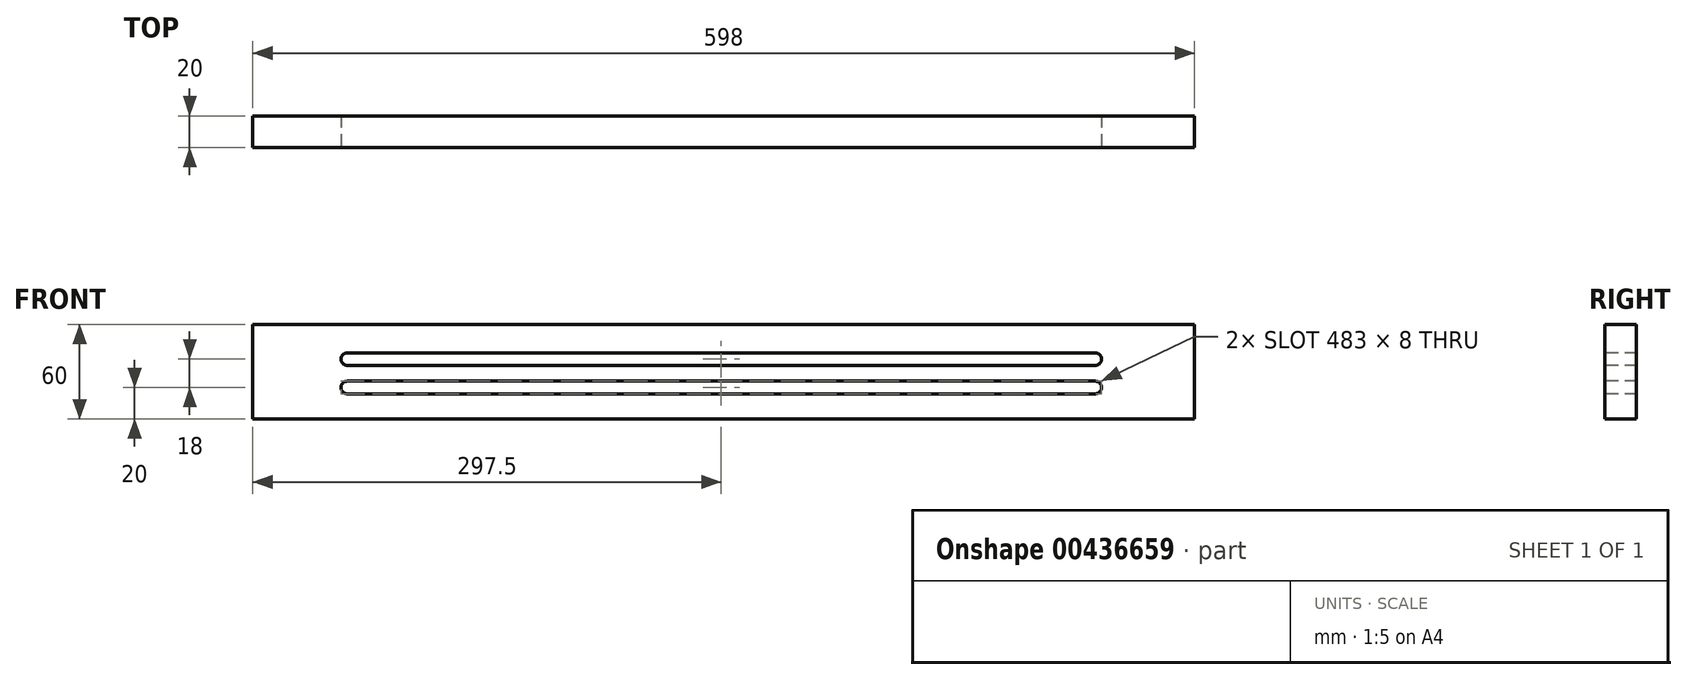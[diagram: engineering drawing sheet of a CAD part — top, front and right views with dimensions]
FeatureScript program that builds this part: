
annotation { "Feature Type Name" : "Feature", "Feature Type Description" : "" }
export const myFeature = defineFeature(function(context is Context, id is Id, definition is map)
    precondition{}
    {
        {
            var Q0;
            Q0=qCreatedBy(makeId("Right.planeOp"),FACE);
            var sketch = newSketch(context, id + "F0", { "sketchPlane" : qUnion([Q0])});
            skLineSegment(sketch, "E0.bottom", {"start": v(10, -30) * mm, "end": v(-10, -30) * mm});
            skLineSegment(sketch, "E0.top", {"start": v(10, 30) * mm, "end": v(-10, 30) * mm});
            skLineSegment(sketch, "E0.left", {"start": v(10, -30) * mm, "end": v(10, 30) * mm});
            skLineSegment(sketch, "E0.right", {"start": v(-10, -30) * mm, "end": v(-10, 30) * mm});
            skPoint(sketch, "E0.middle", {"position": v(0, 0) * mm});
            skSolve(sketch);
        }
        {
            var Q0;
            Q0=qSketchRegion(id+"F0",true);
            extrude(context, id + "F1", {"entities" : qUnion([Q0]), "depth" : 598 * mm});
        }
        {
            var Q0;
            Q0=makeQuery(id+"F1.opExtrude","SWEPT_FACE",FACE,{"disambiguationData":[OSD([sQuery(id+"F0.wireOp",EDGE,"E0.right")])]});
            var sketch = newSketch(context, id + "F2", { "sketchPlane" : qUnion([Q0])});
            skLineSegment(sketch, "E1.bottom", {"start": v(60, 12) * mm, "end": v(535, 12) * mm});
            skLineSegment(sketch, "E1.top", {"start": v(60, 4) * mm, "end": v(535, 4) * mm});
            skArc(sketch, "E2", {"start": v(60, 12) * mm, "mid": v(56, 8) * mm, "end": v(60, 4) * mm});
            skArc(sketch, "E3", {"start": v(535, 4) * mm, "mid": v(539, 8) * mm, "end": v(535, 12) * mm});
            skArc(sketch, "E4.0.1.0", {"start": v(60, -6) * mm, "mid": v(56, -10) * mm, "end": v(60, -14) * mm});
            skLineSegment(sketch, "E4.0.1.1", {"start": v(60, -6) * mm, "end": v(535, -6) * mm});
            skLineSegment(sketch, "E4.0.1.2", {"start": v(60, -14) * mm, "end": v(535, -14) * mm});
            skArc(sketch, "E4.0.1.3", {"start": v(535, -14) * mm, "mid": v(539, -10) * mm, "end": v(535, -6) * mm});
            skLineSegment(sketch, "E4.direction1", {"start": v(60, 4) * mm, "end": v(85, 4) * mm, "construction": true});
            skLineSegment(sketch, "E4.direction2", {"start": v(60, 4) * mm, "end": v(60, -14) * mm, "construction": true});
            skSolve(sketch);
        }
        {
            var Q0;
            Q0 = qSketchRegion(id + "F2", true);
            extrude(context, id + "F3", {"entities" : qUnion([Q0]), "operationType" : NewBodyOperationType.REMOVE, "oppositeDirection" : true, "depth" : 25 * mm});
        }
    });
